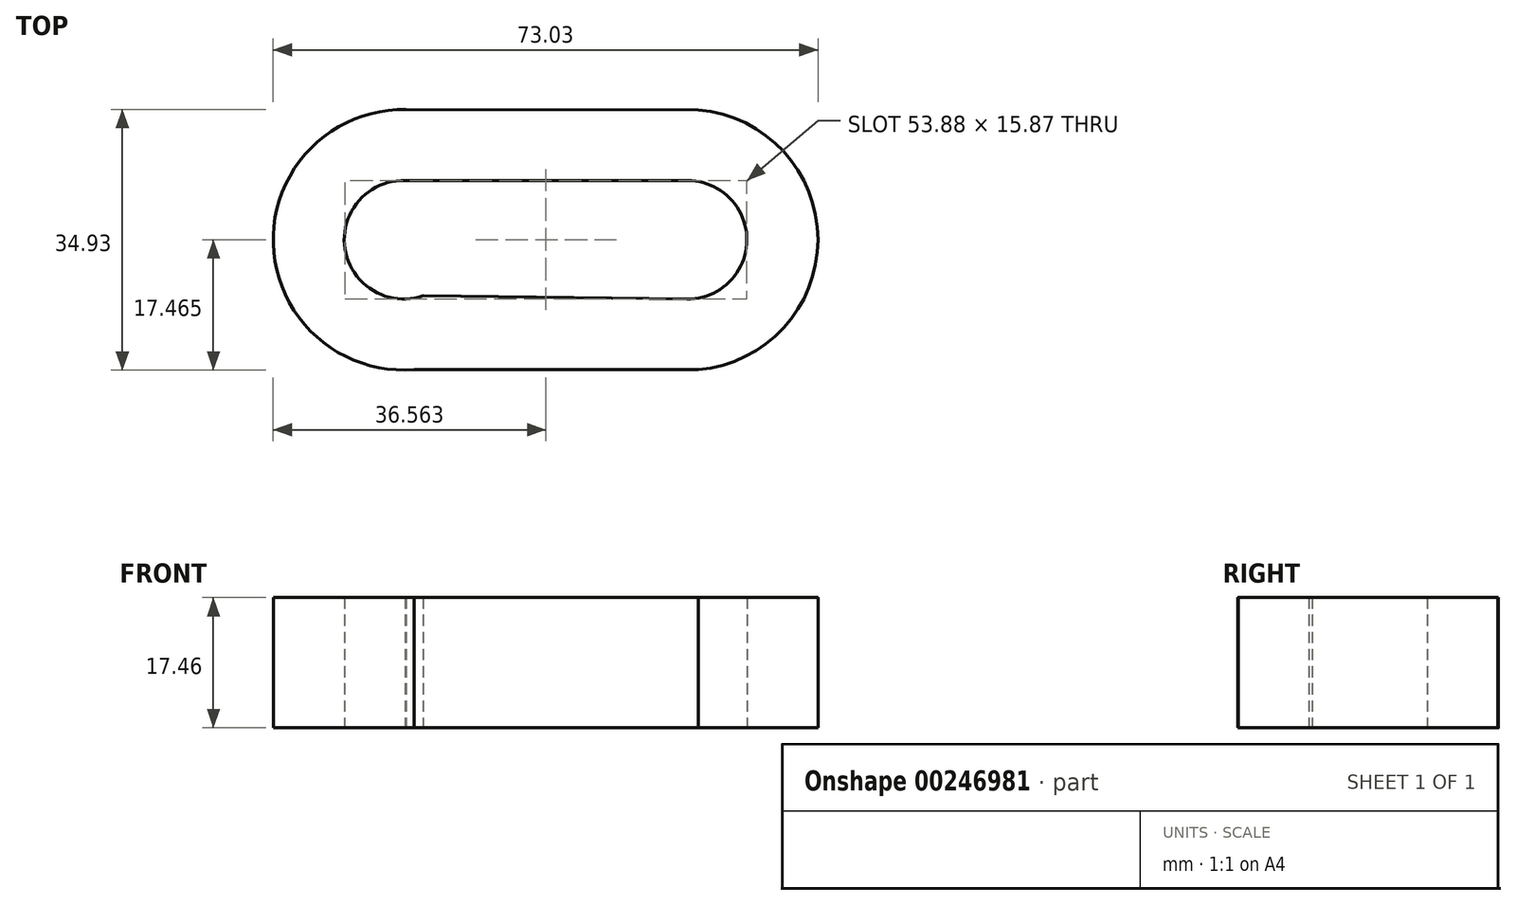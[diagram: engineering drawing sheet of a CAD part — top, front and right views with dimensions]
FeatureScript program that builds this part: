
annotation { "Feature Type Name" : "Feature", "Feature Type Description" : "" }
export const myFeature = defineFeature(function(context is Context, id is Id, definition is map)
    precondition{}
    {
        {
            var Q0;
            Q0=qCreatedBy(makeId("Top.planeOp"),FACE);
            var sketch = newSketch(context, id + "F0", { "sketchPlane" : qUnion([Q0])});
            skArc(sketch, "E0", {"start": v(26.44, -39.82) * mm, "mid": v(45.32, -22.44) * mm, "end": v(26.49, -5) * mm});
            skArc(sketch, "E1", {"start": v(27.76, -30.35) * mm, "mid": v(35.8, -22.47) * mm, "end": v(27.85, -14.48) * mm});
            skArc(sketch, "E2", {"start": v(-10.03, -14.48) * mm, "mid": v(-18.09, -23.64) * mm, "end": v(-7.62, -29.9) * mm});
            skArc(sketch, "E3", {"start": v(-9.89, -4.96) * mm, "mid": v(-27.7, -22.95) * mm, "end": v(-8.83, -39.82) * mm});
            skLineSegment(sketch, "E4", {"start": v(-9.89, -4.96) * mm, "end": v(29.27, -5.01) * mm});
            skLineSegment(sketch, "E5", {"start": v(-8.83, -39.82) * mm, "end": v(29.27, -39.82) * mm});
            skLineSegment(sketch, "E6", {"start": v(-10.46, -14.48) * mm, "end": v(29.27, -14.48) * mm});
            skLineSegment(sketch, "E7", {"start": v(-7.62, -29.9) * mm, "end": v(29.27, -30.37) * mm});
            skSolve(sketch);
        }
        {
            var Q0;
            {var subQ1=sQuery(id+"F0.wireOp",EDGE,"E1");Q0=makeQuery(id+"F0.imprint","IMPRINT",FACE,{"disambiguationData":[TD([[makeQuery(id+"F0.imprint","IMPRINT",EDGE,{"derivedFrom":subQ1}),-1.0]])]});}
            extrude(context, id + "F1", {"entities" : qUnion([Q0]), "depth" : 17.46 * mm});
        }
    });
